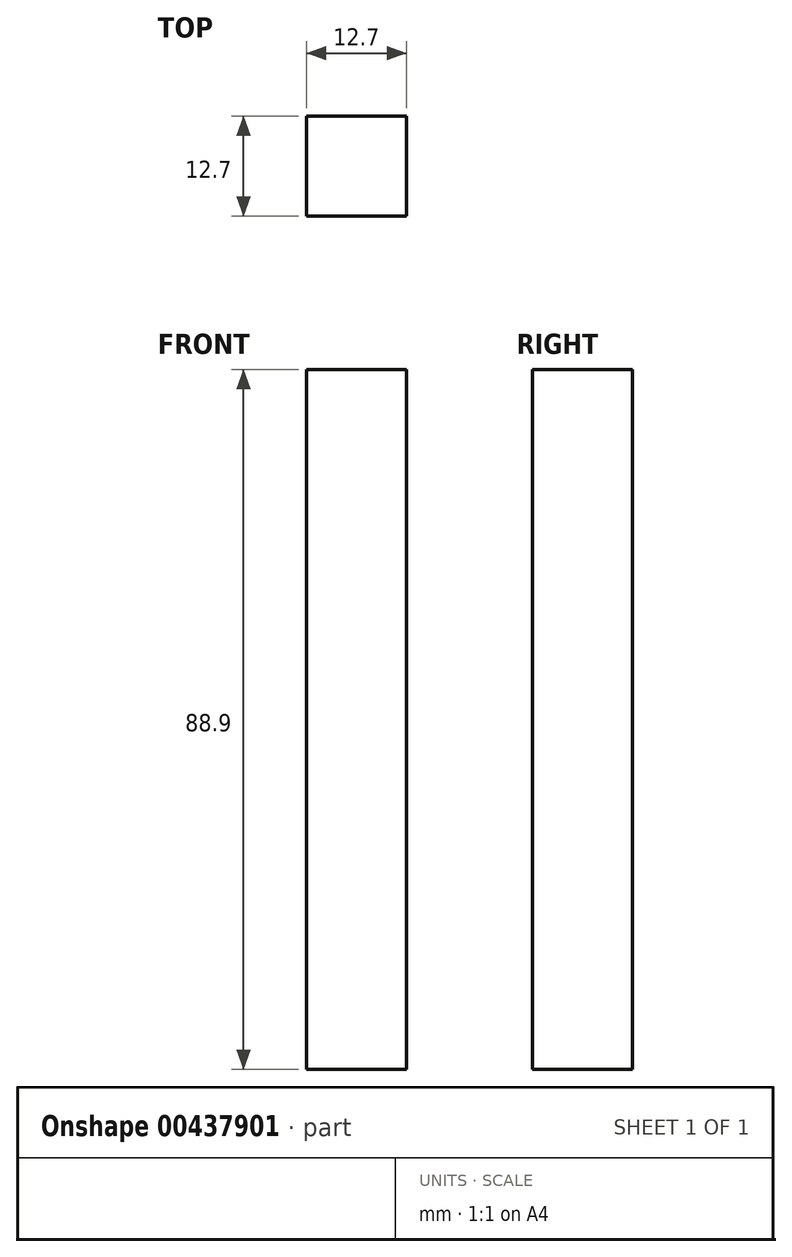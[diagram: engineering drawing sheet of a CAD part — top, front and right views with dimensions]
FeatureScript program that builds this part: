
annotation { "Feature Type Name" : "Feature", "Feature Type Description" : "" }
export const myFeature = defineFeature(function(context is Context, id is Id, definition is map)
    precondition{}
    {
        {
            var Q0;
            Q0=qCreatedBy(makeId("Top.planeOp"),FACE);
            var sketch = newSketch(context, id + "F0", { "sketchPlane" : qUnion([Q0])});
            skLineSegment(sketch, "E0.bottom", {"start": v(-50.92, 26.67) * mm, "end": v(-38.22, 26.67) * mm});
            skLineSegment(sketch, "E0.top", {"start": v(-50.92, 13.97) * mm, "end": v(-38.22, 13.97) * mm});
            skLineSegment(sketch, "E0.left", {"start": v(-50.92, 26.67) * mm, "end": v(-50.92, 13.97) * mm});
            skLineSegment(sketch, "E0.right", {"start": v(-38.22, 26.67) * mm, "end": v(-38.22, 13.97) * mm});
            skSolve(sketch);
        }
        {
            var Q0;
            Q0=makeQuery(id+"F0.imprint","IMPRINT",FACE,{"disambiguationData":[TD([[makeQuery(id+"F0.imprint","IMPRINT",EDGE,{"derivedFrom":sQuery(id+"F0.wireOp",EDGE,"E0.bottom")}),-1.0]])]});
            extrude(context, id + "F1", {"entities" : qUnion([Q0]), "depth" : 88.9 * mm});
        }
    });
